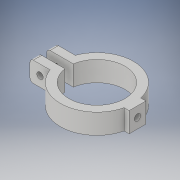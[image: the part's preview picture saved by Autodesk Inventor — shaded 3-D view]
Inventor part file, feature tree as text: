
AUTODESK INVENTOR PART (.ipt)
format: ipt  version: 2019 (Build 230136000, 136)  size: 176,128 bytes
history: native  units: in
note: dims shown in document units (in); Inventor stores cm internally (conversion verified against a paired STEP export)
features: sketch x5, extrude x3, hole x3, fillet x1, plane x1
ambient origin geometry x8: Origin, YZ Plane, XZ Plane, XY Plane, X Axis, Y Axis, Z Axis, Center Point
bodies: Solid1 (feature_tree)
feature tree (13):
  extrude  "Extrusion1"  Depth=0.1969in
  hole  "Hole1"  [1 undecoded]
  extrude  "Extrusion2"  Depth=0.3937in
  fillet  "Fillet1"  Radius=0.4724in
  plane  "Work Plane3"
  sketch  "Sketch5"  dims[d10=0.1495in d11=0.2362in d12=0.279in d13=0.0787in d14=0.5635in d15=0.315in d16=0.8108in d17=0.3159in]
  extrude  "Extrusion4"  Depth=0.3159in
  hole  "Hole2"  [1 undecoded]
  hole  "Hole3"  [1 undecoded]
  sketch  "Sketch1"  dims[d0=1.3189in d1=0.1969in]
  sketch  "Sketch2"  dims[d4=0.1969in d5=0.1969in]
  sketch  "Sketch3"  dims[d6=0.3937in d7=0.4724in d8=0.4724in d9=0.0in]
  sketch  "Sketch6"  dims[d18=0.106in d19=0.0in d20=0.0787in d24=0.7776in d25=0.2559in d26=0.106in d27=0.0in d28=0.1495in d29=0.2362in d30=0.279in d31=0.0787in d32=0.5635in d33=0.315in d34=0.8108in d35=0.3937in d36=0.1181in d37=0.104in d38=0.276in d39=0.279in d40=0.0787in d41=0.5635in d42=0.4322in d43=0.8108in d44=0.0295in d45=0.8108in d46=0.0025in d47=0.0295in d48=0.0148in]
note: 3 required parameter values undecoded (feature->parameter linkage not recoverable at this tier; creation-order binding heuristic only, values carry confidence <= 0.55)
